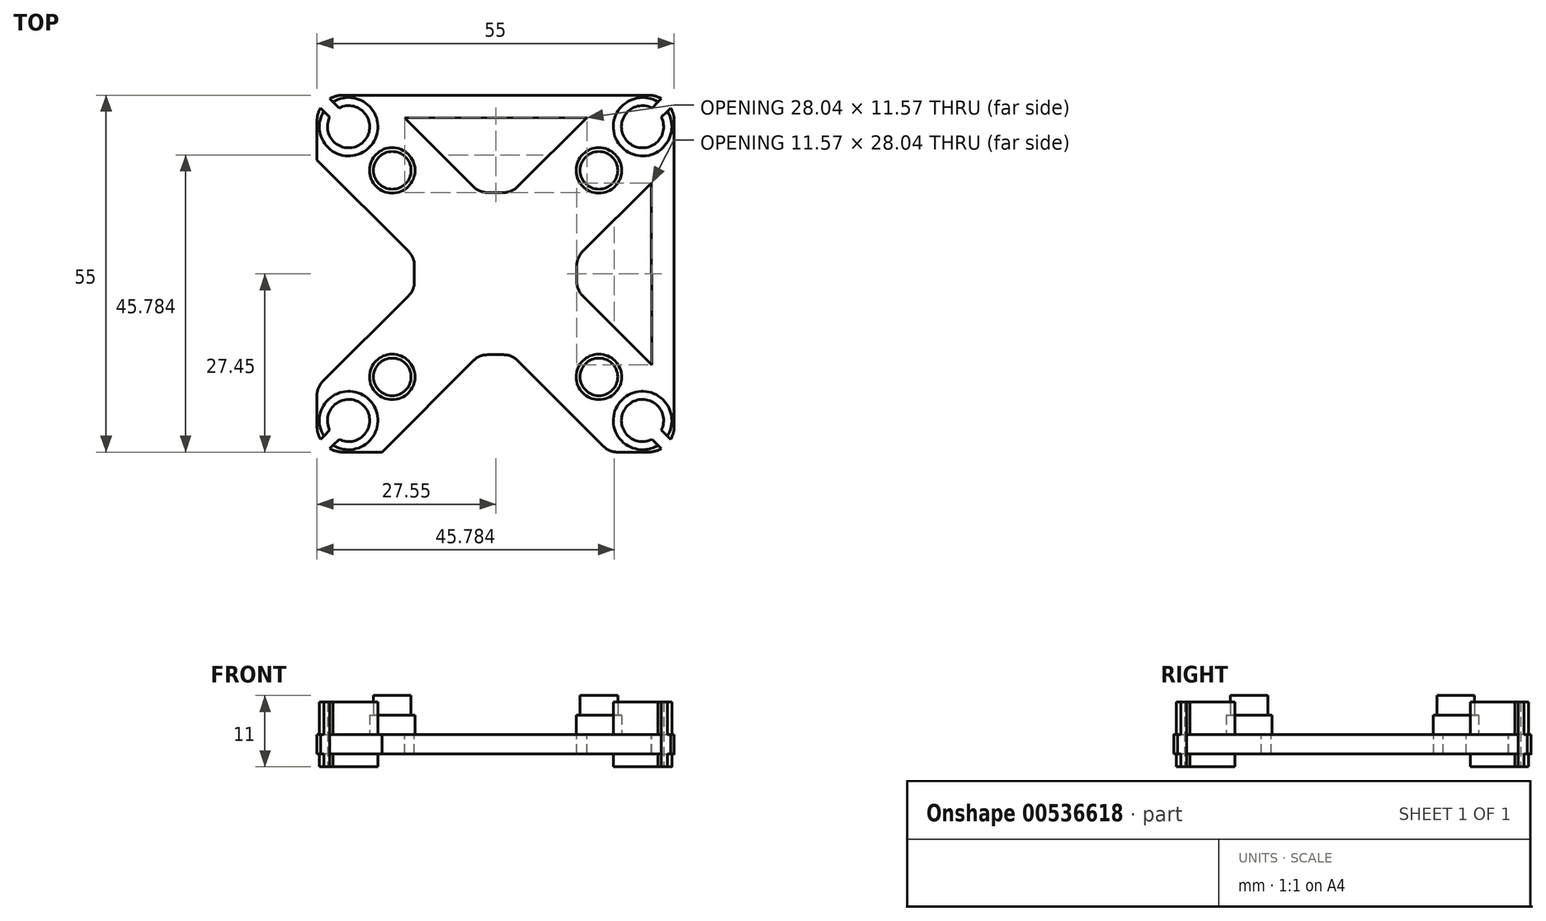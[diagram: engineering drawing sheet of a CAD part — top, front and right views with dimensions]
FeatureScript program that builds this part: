
annotation { "Feature Type Name" : "Feature", "Feature Type Description" : "" }
export const myFeature = defineFeature(function(context is Context, id is Id, definition is map)
    precondition{}
    {
        {
            var Q0;
            Q0=qCreatedBy(makeId("Top.planeOp"),FACE);
            var sketch = newSketch(context, id + "F0", { "sketchPlane" : qUnion([Q0])});
            skLineSegment(sketch, "E0.bottom", {"start": v(-27.5, 27.5) * mm, "end": v(27.5, 27.5) * mm});
            skLineSegment(sketch, "E0.top", {"start": v(-27.5, -27.5) * mm, "end": v(27.5, -27.5) * mm});
            skLineSegment(sketch, "E0.left", {"start": v(-27.5, 27.5) * mm, "end": v(-27.5, -27.5) * mm});
            skLineSegment(sketch, "E0.right", {"start": v(27.5, 27.5) * mm, "end": v(27.5, -27.5) * mm});
            skPoint(sketch, "E0.middle", {"position": v(0, 0) * mm});
            skLineSegment(sketch, "E1", {"start": v(-27.5, 27.5) * mm, "end": v(27.5, -27.5) * mm, "construction": true});
            skLineSegment(sketch, "E2", {"start": v(27.5, 27.5) * mm, "end": v(-27.5, -27.5) * mm, "construction": true});
            skSolve(sketch);
        }
        {
            var Q0;
            Q0 = qSketchRegion(id + "F0", true);
            extrude(context, id + "F1", {"entities" : qUnion([Q0]), "depth" : 3 * mm, "offsetDistance" : 25 * mm});
        }
        {
            var Q0;
            Q0=makeQuery(id+"F1.opExtrude","CAP_FACE",FACE,{"disambiguationData":[OSD([sQuery(id+"F0.wireOp",EDGE,"E0.bottom"),sQuery(id+"F0.wireOp",EDGE,"E0.top"),sQuery(id+"F0.wireOp",EDGE,"E0.left"),sQuery(id+"F0.wireOp",EDGE,"E0.right")])],"isStart":false});
            var sketch = newSketch(context, id + "F2", { "sketchPlane" : qUnion([Q0])});
            skLineSegment(sketch, "E3", {"start": v(-27.5, 27.5) * mm, "end": v(27.5, -27.5) * mm, "construction": true});
            skLineSegment(sketch, "E4", {"start": v(27.5, 27.5) * mm, "end": v(-27.5, -27.5) * mm, "construction": true});
            skCircle(sketch, "E5", {"center": v(-15.9, 15.9) * mm, "radius": 3.5 * mm});
            skCircle(sketch, "E6", {"center": v(15.9, 15.9) * mm, "radius": 3.5 * mm});
            skCircle(sketch, "E7", {"center": v(-15.9, -15.9) * mm, "radius": 3.5 * mm});
            skCircle(sketch, "E8", {"center": v(15.9, -15.9) * mm, "radius": 3.5 * mm});
            skSolve(sketch);
        }
        {
            var Q0;
            Q0 = qSketchRegion(id + "F2", true);
            extrude(context, id + "F3", {"entities" : qUnion([Q0]), "operationType" : NewBodyOperationType.ADD, "depth" : 3 * mm, "offsetDistance" : 25 * mm});
        }
        {
            var Q0;
            Q0=makeQuery(id+"F3.opExtrude","CAP_FACE",FACE,{"disambiguationData":[OSD([sQuery(id+"F2.wireOp",EDGE,"E5")])],"isStart":false});
            var sketch = newSketch(context, id + "F4", { "sketchPlane" : qUnion([Q0])});
            skCircle(sketch, "E9", {"center": v(-15.9, 15.9) * mm, "radius": 2.9 * mm});
            skCircle(sketch, "E10", {"center": v(15.9, 15.9) * mm, "radius": 2.9 * mm});
            skCircle(sketch, "E11", {"center": v(-15.9, -15.9) * mm, "radius": 2.9 * mm});
            skCircle(sketch, "E12", {"center": v(15.9, -15.9) * mm, "radius": 2.9 * mm});
            skSolve(sketch);
        }
        {
            var Q0;
            Q0 = qSketchRegion(id + "F4", true);
            extrude(context, id + "F5", {"entities" : qUnion([Q0]), "operationType" : NewBodyOperationType.ADD, "depth" : 3 * mm, "offsetDistance" : 25 * mm});
        }
        {
            var Q0;
            Q0=makeQuery(id+"F1.opExtrude","CAP_FACE",FACE,{"disambiguationData":[OSD([sQuery(id+"F0.wireOp",EDGE,"E0.bottom"),sQuery(id+"F0.wireOp",EDGE,"E0.top"),sQuery(id+"F0.wireOp",EDGE,"E0.left"),sQuery(id+"F0.wireOp",EDGE,"E0.right")])],"isStart":false});
            var sketch = newSketch(context, id + "F6", { "sketchPlane" : qUnion([Q0])});
            skLineSegment(sketch, "E13", {"start": v(-27.5, 27.5) * mm, "end": v(27.5, -27.5) * mm, "construction": true});
            skLineSegment(sketch, "E14", {"start": v(27.5, 27.5) * mm, "end": v(-27.5, -27.5) * mm, "construction": true});
            skCircle(sketch, "E15", {"center": v(-22.63, 22.63) * mm, "radius": 4.5 * mm});
            skCircle(sketch, "E16", {"center": v(22.63, 22.63) * mm, "radius": 4.5 * mm});
            skCircle(sketch, "E17", {"center": v(22.63, -22.63) * mm, "radius": 4.5 * mm});
            skCircle(sketch, "E18", {"center": v(-22.63, -22.63) * mm, "radius": 4.5 * mm});
            skSolve(sketch);
        }
        {
            var Q0;
            Q0 = qSketchRegion(id + "F6", true);
            extrude(context, id + "F7", {"entities" : qUnion([Q0]), "operationType" : NewBodyOperationType.ADD, "endBound" : BoundingType.SYMMETRIC, "oppositeDirection" : true, "depth" : 10 * mm, "offsetDistance" : 25 * mm});
        }
        {
            var Q0;
            Q0=makeQuery(id+"F7.opExtrude","CAP_FACE",FACE,{"disambiguationData":[OSD([sQuery(id+"F6.wireOp",EDGE,"E18")])],"isStart":false});
            var sketch = newSketch(context, id + "F8", { "sketchPlane" : qUnion([Q0])});
            skCircle(sketch, "E19", {"center": v(-22.63, 22.63) * mm, "radius": 3.25 * mm});
            skCircle(sketch, "E20", {"center": v(22.63, 22.63) * mm, "radius": 3.25 * mm});
            skCircle(sketch, "E21", {"center": v(-22.63, -22.63) * mm, "radius": 3.25 * mm});
            skCircle(sketch, "E22", {"center": v(22.63, -22.63) * mm, "radius": 3.25 * mm});
            skSolve(sketch);
        }
        {
            var Q0;
            Q0 = qSketchRegion(id + "F8", true);
            extrude(context, id + "F9", {"entities" : qUnion([Q0]), "operationType" : NewBodyOperationType.REMOVE, "endBound" : BoundingType.SYMMETRIC, "oppositeDirection" : true, "depth" : 50 * mm, "offsetDistance" : 25 * mm});
        }
        {
            var Q0;
            Q0=makeQuery(id+"F1.opExtrude","SWEPT_EDGE",EDGE,{"disambiguationData":[OSD([sQuery(id+"F0.wireOp",EDGE,"E0.top"),sQuery(id+"F0.wireOp",EDGE,"E0.right")])]});
            var Q1;
            Q1=makeQuery(id+"F1.opExtrude","SWEPT_EDGE",EDGE,{"disambiguationData":[OSD([sQuery(id+"F0.wireOp",EDGE,"E0.top"),sQuery(id+"F0.wireOp",EDGE,"E0.left")])]});
            var Q2;
            Q2=makeQuery(id+"F1.opExtrude","SWEPT_EDGE",EDGE,{"disambiguationData":[OSD([sQuery(id+"F0.wireOp",EDGE,"E0.bottom"),sQuery(id+"F0.wireOp",EDGE,"E0.left")])]});
            var Q3;
            Q3=makeQuery(id+"F1.opExtrude","SWEPT_EDGE",EDGE,{"disambiguationData":[OSD([sQuery(id+"F0.wireOp",EDGE,"E0.bottom"),sQuery(id+"F0.wireOp",EDGE,"E0.right")])]});
            fillet(context, id + "F10", {"entities" : qUnion([Q0, Q1, Q2, Q3]), "radius" : 4 * mm, "tangentPropagation" : true, "allowEdgeOverflow" : false});
        }
        {
            var Q0;
            Q0=makeQuery(id+"F1.opExtrude","CAP_FACE",FACE,{"disambiguationData":[OSD([sQuery(id+"F0.wireOp",EDGE,"E0.bottom"),sQuery(id+"F0.wireOp",EDGE,"E0.top"),sQuery(id+"F0.wireOp",EDGE,"E0.left"),sQuery(id+"F0.wireOp",EDGE,"E0.right")])],"isStart":false});
            var sketch = newSketch(context, id + "F11", { "sketchPlane" : qUnion([Q0])});
            skLineSegment(sketch, "E23.0", {"start": v(-27.5, 27.5) * mm, "end": v(27.5, -27.5) * mm, "construction": true});
            skLineSegment(sketch, "E24.0", {"start": v(27.5, 27.5) * mm, "end": v(-27.5, -27.5) * mm, "construction": true});
            skLineSegment(sketch, "E25.bottom", {"start": v(12.5, -12.5) * mm, "end": v(-12.5, -12.5) * mm, "construction": true});
            skLineSegment(sketch, "E25.top", {"start": v(12.5, 12.5) * mm, "end": v(-12.5, 12.5) * mm, "construction": true});
            skLineSegment(sketch, "E25.left", {"start": v(12.5, -12.5) * mm, "end": v(12.5, 12.5) * mm, "construction": true});
            skLineSegment(sketch, "E25.right", {"start": v(-12.5, -12.5) * mm, "end": v(-12.5, 12.5) * mm, "construction": true});
            skPoint(sketch, "E25.middle", {"position": v(0, 0) * mm});
            skPoint(sketch, "E26", {"position": v(-27.5, 17.5) * mm});
            skLineSegment(sketch, "E27", {"start": v(-27.5, 17.5) * mm, "end": v(-12.5, 2.5) * mm});
            skPoint(sketch, "E28", {"position": v(-27.5, -17.5) * mm});
            skLineSegment(sketch, "E29", {"start": v(-27.5, -17.5) * mm, "end": v(-12.5, -2.5) * mm});
            skLineSegment(sketch, "E30", {"start": v(-12.5, 2.5) * mm, "end": v(-12.5, -2.5) * mm});
            skLineSegment(sketch, "E31", {"start": v(-27.5, 17.5) * mm, "end": v(-27.5, -17.5) * mm});
            skLineSegment(sketch, "E32.1.0", {"start": v(-17.5, -27.5) * mm, "end": v(17.5, -27.5) * mm});
            skLineSegment(sketch, "E32.1.1", {"start": v(-17.5, -27.5) * mm, "end": v(-2.5, -12.5) * mm});
            skLineSegment(sketch, "E32.1.2", {"start": v(17.5, -27.5) * mm, "end": v(2.5, -12.5) * mm});
            skLineSegment(sketch, "E32.2.0", {"start": v(27.5, -17.5) * mm, "end": v(27.5, 17.5) * mm});
            skLineSegment(sketch, "E32.2.1", {"start": v(27.5, -17.5) * mm, "end": v(12.5, -2.5) * mm});
            skLineSegment(sketch, "E32.2.2", {"start": v(27.5, 17.5) * mm, "end": v(12.5, 2.5) * mm});
            skLineSegment(sketch, "E32.3.0", {"start": v(17.5, 27.5) * mm, "end": v(-17.5, 27.5) * mm});
            skLineSegment(sketch, "E32.3.1", {"start": v(17.5, 27.5) * mm, "end": v(2.5, 12.5) * mm});
            skLineSegment(sketch, "E32.3.2", {"start": v(-17.5, 27.5) * mm, "end": v(-2.5, 12.5) * mm});
            skLineSegment(sketch, "E33", {"start": v(-2.5, 12.5) * mm, "end": v(2.5, 12.5) * mm});
            skLineSegment(sketch, "E34", {"start": v(12.5, 2.5) * mm, "end": v(12.5, -2.5) * mm});
            skLineSegment(sketch, "E35", {"start": v(2.5, -12.5) * mm, "end": v(-2.5, -12.5) * mm});
            skSolve(sketch);
        }
        {
            var Q0;
            Q0 = qSketchRegion(id + "F11", true);
            extrude(context, id + "F12", {"entities" : qUnion([Q0]), "operationType" : NewBodyOperationType.REMOVE, "endBound" : BoundingType.SYMMETRIC, "oppositeDirection" : true, "depth" : 50 * mm, "offsetDistance" : 25 * mm});
        }
        {
            var Q0;
            Q0=makeQuery(id+"F12.boolean.opBoolean","COPY",EDGE,{"derivedFrom":makeQuery(id+"F12.opExtrude","SWEPT_EDGE",EDGE,{"disambiguationData":[OSD([sQuery(id+"F0.wireOp",EDGE,"E0.right"),sQuery(id+"F11.wireOp",EDGE,"E32.2.0"),sQuery(id+"F11.wireOp",EDGE,"E32.2.2")])]})});
            var Q1;
            Q1=makeQuery(id+"F12.boolean.opBoolean","COPY",EDGE,{"derivedFrom":makeQuery(id+"F12.opExtrude","SWEPT_EDGE",EDGE,{"disambiguationData":[OSD([sQuery(id+"F11.wireOp",EDGE,"E32.2.2"),sQuery(id+"F11.wireOp",EDGE,"E34")])]})});
            var Q2;
            Q2=makeQuery(id+"F12.boolean.opBoolean","COPY",EDGE,{"derivedFrom":makeQuery(id+"F12.opExtrude","SWEPT_EDGE",EDGE,{"disambiguationData":[OSD([sQuery(id+"F0.wireOp",EDGE,"E0.right"),sQuery(id+"F11.wireOp",EDGE,"E32.2.0"),sQuery(id+"F11.wireOp",EDGE,"E32.2.1")])]})});
            var Q3;
            Q3=makeQuery(id+"F12.boolean.opBoolean","COPY",EDGE,{"derivedFrom":makeQuery(id+"F12.opExtrude","SWEPT_EDGE",EDGE,{"disambiguationData":[OSD([sQuery(id+"F0.wireOp",EDGE,"E0.top"),sQuery(id+"F11.wireOp",EDGE,"E32.1.0"),sQuery(id+"F11.wireOp",EDGE,"E32.1.2")])]})});
            var Q4;
            Q4=makeQuery(id+"F12.boolean.opBoolean","COPY",EDGE,{"derivedFrom":makeQuery(id+"F12.opExtrude","SWEPT_EDGE",EDGE,{"disambiguationData":[OSD([sQuery(id+"F0.wireOp",EDGE,"E0.top"),sQuery(id+"F11.wireOp",EDGE,"E32.1.0"),sQuery(id+"F11.wireOp",EDGE,"E32.1.1")])]})});
            var Q5;
            Q5=makeQuery(id+"F12.boolean.opBoolean","COPY",EDGE,{"derivedFrom":makeQuery(id+"F12.opExtrude","SWEPT_EDGE",EDGE,{"disambiguationData":[OSD([sQuery(id+"F11.wireOp",EDGE,"E32.1.1"),sQuery(id+"F11.wireOp",EDGE,"E35")])]})});
            var Q6;
            Q6=makeQuery(id+"F12.boolean.opBoolean","COPY",EDGE,{"derivedFrom":makeQuery(id+"F12.opExtrude","SWEPT_EDGE",EDGE,{"disambiguationData":[OSD([sQuery(id+"F11.wireOp",EDGE,"E32.1.2"),sQuery(id+"F11.wireOp",EDGE,"E35")])]})});
            var Q7;
            Q7=makeQuery(id+"F12.boolean.opBoolean","COPY",EDGE,{"derivedFrom":makeQuery(id+"F12.opExtrude","SWEPT_EDGE",EDGE,{"disambiguationData":[OSD([sQuery(id+"F0.wireOp",EDGE,"E0.left"),sQuery(id+"F11.wireOp",EDGE,"E29"),sQuery(id+"F11.wireOp",EDGE,"E31")])]})});
            var Q8;
            Q8=makeQuery(id+"F12.boolean.opBoolean","COPY",EDGE,{"derivedFrom":makeQuery(id+"F12.opExtrude","SWEPT_EDGE",EDGE,{"disambiguationData":[OSD([sQuery(id+"F11.wireOp",EDGE,"E29"),sQuery(id+"F11.wireOp",EDGE,"E30")])]})});
            var Q9;
            Q9=makeQuery(id+"F12.boolean.opBoolean","COPY",EDGE,{"derivedFrom":makeQuery(id+"F12.opExtrude","SWEPT_EDGE",EDGE,{"disambiguationData":[OSD([sQuery(id+"F11.wireOp",EDGE,"E27"),sQuery(id+"F11.wireOp",EDGE,"E30")])]})});
            var Q10;
            Q10=makeQuery(id+"F12.boolean.opBoolean","COPY",EDGE,{"derivedFrom":makeQuery(id+"F12.opExtrude","SWEPT_EDGE",EDGE,{"disambiguationData":[OSD([sQuery(id+"F0.wireOp",EDGE,"E0.left"),sQuery(id+"F11.wireOp",EDGE,"E27"),sQuery(id+"F11.wireOp",EDGE,"E31")])]})});
            var Q11;
            Q11=makeQuery(id+"F12.boolean.opBoolean","COPY",EDGE,{"derivedFrom":makeQuery(id+"F12.opExtrude","SWEPT_EDGE",EDGE,{"disambiguationData":[OSD([sQuery(id+"F0.wireOp",EDGE,"E0.bottom"),sQuery(id+"F11.wireOp",EDGE,"E32.3.0"),sQuery(id+"F11.wireOp",EDGE,"E32.3.2")])]})});
            var Q12;
            Q12=makeQuery(id+"F12.boolean.opBoolean","COPY",EDGE,{"derivedFrom":makeQuery(id+"F12.opExtrude","SWEPT_EDGE",EDGE,{"disambiguationData":[OSD([sQuery(id+"F11.wireOp",EDGE,"E32.3.2"),sQuery(id+"F11.wireOp",EDGE,"E33")])]})});
            var Q13;
            Q13=makeQuery(id+"F12.boolean.opBoolean","COPY",EDGE,{"derivedFrom":makeQuery(id+"F12.opExtrude","SWEPT_EDGE",EDGE,{"disambiguationData":[OSD([sQuery(id+"F11.wireOp",EDGE,"E32.3.1"),sQuery(id+"F11.wireOp",EDGE,"E33")])]})});
            var Q14;
            Q14=makeQuery(id+"F12.boolean.opBoolean","COPY",EDGE,{"derivedFrom":makeQuery(id+"F12.opExtrude","SWEPT_EDGE",EDGE,{"disambiguationData":[OSD([sQuery(id+"F0.wireOp",EDGE,"E0.bottom"),sQuery(id+"F11.wireOp",EDGE,"E32.3.0"),sQuery(id+"F11.wireOp",EDGE,"E32.3.1")])]})});
            var Q15;
            Q15=makeQuery(id+"F12.boolean.opBoolean","COPY",EDGE,{"derivedFrom":makeQuery(id+"F12.opExtrude","SWEPT_EDGE",EDGE,{"disambiguationData":[OSD([sQuery(id+"F11.wireOp",EDGE,"E32.2.1"),sQuery(id+"F11.wireOp",EDGE,"E34")])]})});
            fillet(context, id + "F13", {"entities" : qUnion([Q0, Q1, Q2, Q3, Q4, Q5, Q6, Q7, Q8, Q9, Q10, Q11, Q12, Q13, Q14, Q15]), "radius" : 3 * mm, "tangentPropagation" : true, "allowEdgeOverflow" : false});
        }
        {
            var Q0;
            Q0=makeQuery(id+"F1.opExtrude","CAP_FACE",FACE,{"disambiguationData":[OSD([sQuery(id+"F0.wireOp",EDGE,"E0.bottom"),sQuery(id+"F0.wireOp",EDGE,"E0.top"),sQuery(id+"F0.wireOp",EDGE,"E0.left"),sQuery(id+"F0.wireOp",EDGE,"E0.right")])],"isStart":false});
            var sketch = newSketch(context, id + "F14", { "sketchPlane" : qUnion([Q0])});
            skLineSegment(sketch, "E36", {"start": v(-27.5, 18.74) * mm, "end": v(-27.5, -18.74) * mm});
            skLineSegment(sketch, "E37", {"start": v(-27.5, -18.74) * mm, "end": v(-23.96, -15.2) * mm});
            skLineSegment(sketch, "E38", {"start": v(-27.5, 18.74) * mm, "end": v(-24.07, 15.1) * mm});
            skLineSegment(sketch, "E39", {"start": v(-24.07, 15.1) * mm, "end": v(-23.96, -15.2) * mm});
            skLineSegment(sketch, "E40.1.0", {"start": v(-18.74, -27.5) * mm, "end": v(-15.1, -24.07) * mm});
            skLineSegment(sketch, "E40.1.1", {"start": v(-18.74, -27.5) * mm, "end": v(18.74, -27.5) * mm});
            skLineSegment(sketch, "E40.1.2", {"start": v(-15.1, -24.07) * mm, "end": v(15.2, -23.96) * mm});
            skLineSegment(sketch, "E40.1.3", {"start": v(18.74, -27.5) * mm, "end": v(15.2, -23.96) * mm});
            skLineSegment(sketch, "E40.2.0", {"start": v(27.5, -18.74) * mm, "end": v(24.07, -15.1) * mm});
            skLineSegment(sketch, "E40.2.1", {"start": v(27.5, -18.74) * mm, "end": v(27.5, 18.74) * mm});
            skLineSegment(sketch, "E40.2.2", {"start": v(24.07, -15.1) * mm, "end": v(23.96, 15.2) * mm});
            skLineSegment(sketch, "E40.2.3", {"start": v(27.5, 18.74) * mm, "end": v(23.96, 15.2) * mm});
            skLineSegment(sketch, "E40.3.0", {"start": v(18.74, 27.5) * mm, "end": v(15.1, 24.07) * mm});
            skLineSegment(sketch, "E40.3.1", {"start": v(18.74, 27.5) * mm, "end": v(-18.74, 27.5) * mm});
            skLineSegment(sketch, "E40.3.2", {"start": v(15.1, 24.07) * mm, "end": v(-15.2, 23.96) * mm});
            skLineSegment(sketch, "E40.3.3", {"start": v(-18.74, 27.5) * mm, "end": v(-15.2, 23.96) * mm});
            skPoint(sketch, "E40.center", {"position": v(0, 0) * mm});
            skSolve(sketch);
        }
        {
            var Q0;
            {var subQ0=sQuery(id+"F0.wireOp",EDGE,"E0.left");var subQ1=sQuery(id+"F0.wireOp",EDGE,"E0.top");var subQ2=makeQuery(id+"F1.opExtrude","CAP_FACE",FACE,{"disambiguationData":[OSD([sQuery(id+"F0.wireOp",EDGE,"E0.bottom"),subQ1,subQ0,sQuery(id+"F0.wireOp",EDGE,"E0.right")])],"isStart":false});var subQ3=subQ2;var subQ4=subQ3;var subQ5=sQuery(id+"F11.wireOp",EDGE,"E31");var subQ12=sQuery(id+"F11.wireOp",EDGE,"E27");var subQ13=makeQuery(id+"F13.opFillet","BLEND_EDGE",EDGE,{"blendedFrom":[makeQuery(id+"F12.boolean.opBoolean","COPY",EDGE,{"derivedFrom":makeQuery(id+"F12.opExtrude","SWEPT_EDGE",EDGE,{"disambiguationData":[OSD([subQ0,subQ12,subQ5])]})}),subQ4],"blendedInto":[subQ4]});Q0=makeQuery(id+"F14.imprint","IMPRINT",FACE,{"disambiguationData":[TD([[makeQuery(id+"F14.imprint","IMPRINT",EDGE,{"derivedFrom":subQ13}),-1.0]])]});}
            var Q1;
            Q1=makeQuery(id+"F14.imprint","IMPRINT",FACE,{"disambiguationData":[TD([[makeQuery(id+"F14.imprint","IMPRINT",EDGE,{"derivedFrom":sQuery(id+"F14.wireOp",EDGE,"E40.3.1")}),1.0]])]});
            var Q2;
            Q2=makeQuery(id+"F14.imprint","IMPRINT",FACE,{"disambiguationData":[TD([[makeQuery(id+"F14.imprint","IMPRINT",EDGE,{"derivedFrom":sQuery(id+"F14.wireOp",EDGE,"E40.2.1")}),1.0]])]});
            var Q3;
            Q3=makeQuery(id+"F14.imprint","IMPRINT",FACE,{"disambiguationData":[TD([[makeQuery(id+"F14.imprint","IMPRINT",EDGE,{"derivedFrom":sQuery(id+"F14.wireOp",EDGE,"E40.1.1")}),1.0]])]});
            var Q4;
            Q4 = qConstructionFilter(qBodyType(qCreatedBy(id + "F14" ,EDGE), BodyType.WIRE), ConstructionObject.NO);
            extrude(context, id + "F15", {"entities" : qUnion([Q0, Q1, Q2, Q3]), "operationType" : NewBodyOperationType.ADD, "surfaceEntities" : qUnion([Q4]), "oppositeDirection" : true, "depth" : 3 * mm, "offsetDistance" : 25 * mm});
        }
        {
            var Q0;
            {var subQ0=sQuery(id+"F0.wireOp",EDGE,"E0.right");var subQ1=sQuery(id+"F0.wireOp",EDGE,"E0.left");var subQ2=sQuery(id+"F0.wireOp",EDGE,"E0.top");var subQ3=sQuery(id+"F0.wireOp",EDGE,"E0.bottom");Q0=makeQuery(id+"F15.boolean.opBoolean","MERGE",FACE,{"derivedFrom":[makeQuery(id+"F1.opExtrude","CAP_FACE",FACE,{"disambiguationData":[OSD([subQ3,subQ2,subQ1,subQ0])],"isStart":false}),makeQuery(id+"F15.opExtrude","CAP_FACE",FACE,{"disambiguationData":[OSD([subQ3,subQ2,subQ1,subQ0,sQuery(id+"F11.wireOp",EDGE,"E27"),sQuery(id+"F11.wireOp",EDGE,"E29"),sQuery(id+"F11.wireOp",EDGE,"E31"),sQuery(id+"F14.wireOp",EDGE,"E36"),sQuery(id+"F14.wireOp",EDGE,"E39")])],"isStart":true}),makeQuery(id+"F15.opExtrude","CAP_FACE",FACE,{"disambiguationData":[OSD([subQ3,subQ2,subQ1,subQ0,sQuery(id+"F11.wireOp",EDGE,"E32.1.0"),sQuery(id+"F11.wireOp",EDGE,"E32.1.1"),sQuery(id+"F11.wireOp",EDGE,"E32.1.2"),sQuery(id+"F14.wireOp",EDGE,"E40.1.1"),sQuery(id+"F14.wireOp",EDGE,"E40.1.2")])],"isStart":true}),makeQuery(id+"F15.opExtrude","CAP_FACE",FACE,{"disambiguationData":[OSD([subQ3,subQ2,subQ1,subQ0,sQuery(id+"F11.wireOp",EDGE,"E32.2.0"),sQuery(id+"F11.wireOp",EDGE,"E32.2.1"),sQuery(id+"F11.wireOp",EDGE,"E32.2.2"),sQuery(id+"F14.wireOp",EDGE,"E40.2.1"),sQuery(id+"F14.wireOp",EDGE,"E40.2.2")])],"isStart":true}),makeQuery(id+"F15.opExtrude","CAP_FACE",FACE,{"disambiguationData":[OSD([subQ3,subQ2,subQ1,subQ0,sQuery(id+"F11.wireOp",EDGE,"E32.3.0"),sQuery(id+"F11.wireOp",EDGE,"E32.3.1"),sQuery(id+"F11.wireOp",EDGE,"E32.3.2"),sQuery(id+"F14.wireOp",EDGE,"E40.3.1"),sQuery(id+"F14.wireOp",EDGE,"E40.3.2")])],"isStart":true})]});}
            var sketch = newSketch(context, id + "F16", { "sketchPlane" : qUnion([Q0])});
            skLineSegment(sketch, "E41.bottom", {"start": v(-25.1, 23.69) * mm, "end": v(-27.93, 26.52) * mm});
            skLineSegment(sketch, "E41.top", {"start": v(-23.69, 25.1) * mm, "end": v(-26.52, 27.93) * mm});
            skLineSegment(sketch, "E41.left", {"start": v(-25.1, 23.69) * mm, "end": v(-23.69, 25.1) * mm});
            skLineSegment(sketch, "E41.right", {"start": v(-27.93, 26.52) * mm, "end": v(-26.52, 27.93) * mm});
            skPoint(sketch, "E41.middle", {"position": v(-25.8, 25.8) * mm});
            skLineSegment(sketch, "E42.1.0", {"start": v(-25.1, -23.69) * mm, "end": v(-27.93, -26.52) * mm});
            skLineSegment(sketch, "E42.1.1", {"start": v(-26.52, -27.93) * mm, "end": v(-27.93, -26.52) * mm});
            skLineSegment(sketch, "E42.1.2", {"start": v(-23.69, -25.1) * mm, "end": v(-26.52, -27.93) * mm});
            skLineSegment(sketch, "E42.1.3", {"start": v(-23.69, -25.1) * mm, "end": v(-25.1, -23.69) * mm});
            skLineSegment(sketch, "E42.2.0", {"start": v(23.69, -25.1) * mm, "end": v(26.52, -27.93) * mm});
            skLineSegment(sketch, "E42.2.1", {"start": v(27.93, -26.52) * mm, "end": v(26.52, -27.93) * mm});
            skLineSegment(sketch, "E42.2.2", {"start": v(25.1, -23.69) * mm, "end": v(27.93, -26.52) * mm});
            skLineSegment(sketch, "E42.2.3", {"start": v(25.1, -23.69) * mm, "end": v(23.69, -25.1) * mm});
            skLineSegment(sketch, "E42.3.0", {"start": v(25.1, 23.69) * mm, "end": v(27.93, 26.52) * mm});
            skLineSegment(sketch, "E42.3.1", {"start": v(26.52, 27.93) * mm, "end": v(27.93, 26.52) * mm});
            skLineSegment(sketch, "E42.3.2", {"start": v(23.69, 25.1) * mm, "end": v(26.52, 27.93) * mm});
            skLineSegment(sketch, "E42.3.3", {"start": v(23.69, 25.1) * mm, "end": v(25.1, 23.69) * mm});
            skPoint(sketch, "E42.center", {"position": v(0, 0) * mm});
            skSolve(sketch);
        }
        {
            var Q0;
            Q0 = qSketchRegion(id + "F16", true);
            extrude(context, id + "F17", {"entities" : qUnion([Q0]), "operationType" : NewBodyOperationType.REMOVE, "endBound" : BoundingType.SYMMETRIC, "oppositeDirection" : true, "depth" : 40 * mm, "offsetDistance" : 25 * mm});
        }
    });
